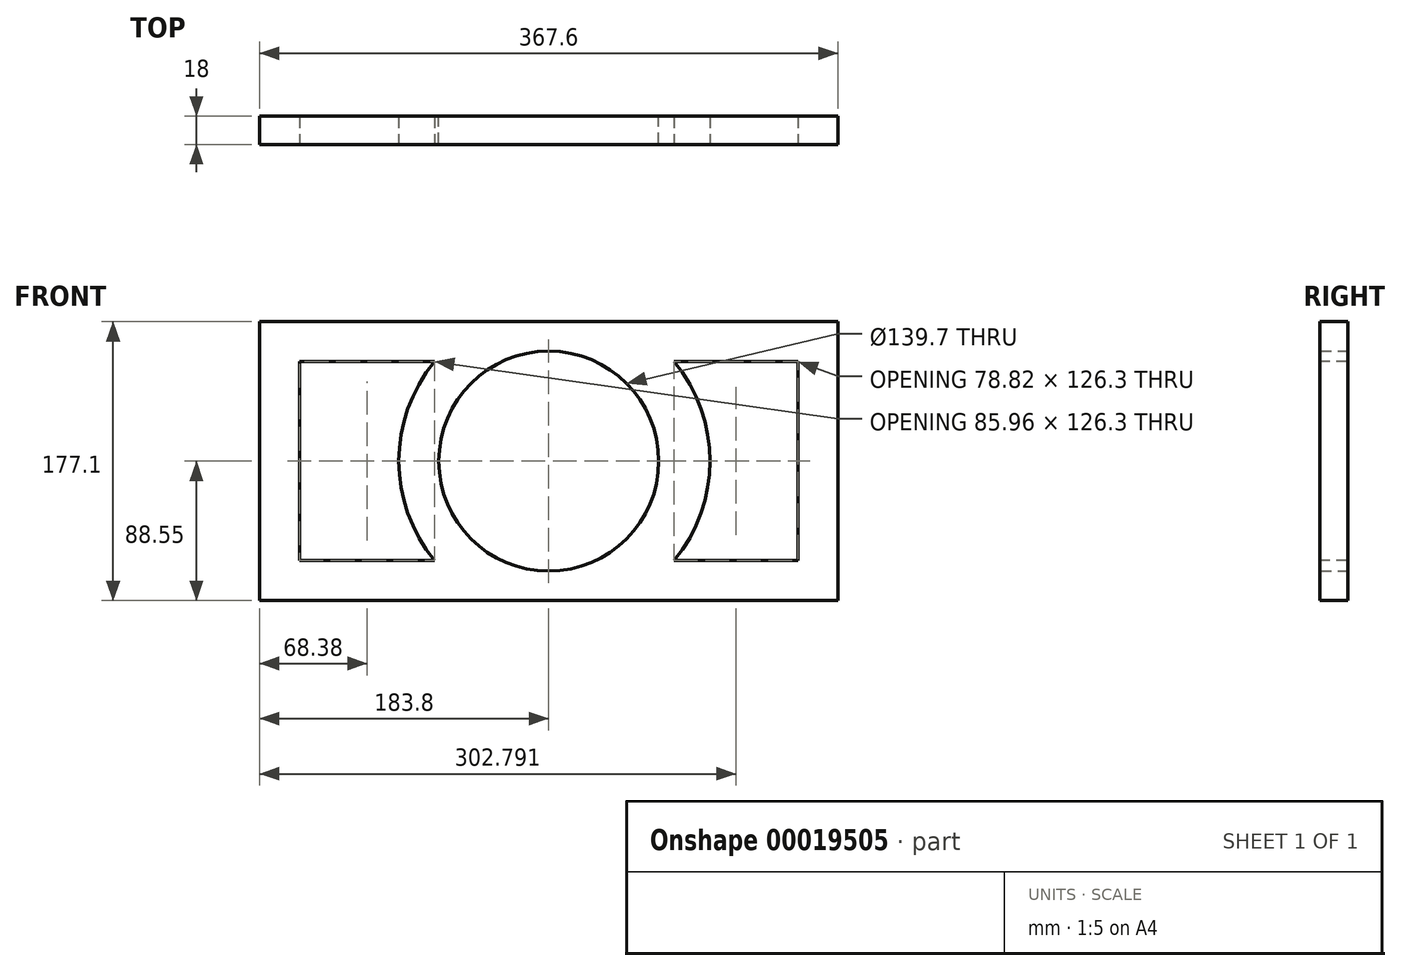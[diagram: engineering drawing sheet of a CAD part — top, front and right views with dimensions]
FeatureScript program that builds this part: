
annotation { "Feature Type Name" : "Feature", "Feature Type Description" : "" }
export const myFeature = defineFeature(function(context is Context, id is Id, definition is map)
    precondition{}
    {
        {
            var Q0;
            Q0=qCreatedBy(makeId("Front.planeOp"),FACE);
            var sketch = newSketch(context, id + "F0", { "sketchPlane" : qUnion([Q0])});
            skLineSegment(sketch, "E0.rect.bottom", {"start": v(183.8, 88.55) * mm, "end": v(-183.8, 88.55) * mm});
            skLineSegment(sketch, "E0.rect.top", {"start": v(183.8, -88.55) * mm, "end": v(-183.8, -88.55) * mm});
            skLineSegment(sketch, "E0.rect.left", {"start": v(183.8, 88.55) * mm, "end": v(183.8, -88.55) * mm});
            skLineSegment(sketch, "E0.rect.right", {"start": v(-183.8, 88.55) * mm, "end": v(-183.8, -88.55) * mm});
            skPoint(sketch, "E0.rect.middle", {"position": v(0, 0) * mm});
            skSolve(sketch);
        }
        {
            var Q0;
            Q0 = qSketchRegion(id + "F0", true);
            extrude(context, id + "F1", {"entities" : qUnion([Q0]), "depth" : 18 * mm});
        }
        {
            var Q0;
            Q0=makeQuery(id+"F1.opExtrude","CAP_FACE",FACE,{"disambiguationData":[OSD([sQuery(id+"F0.wireOp",EDGE,"E0.rect.bottom"),sQuery(id+"F0.wireOp",EDGE,"E0.rect.top"),sQuery(id+"F0.wireOp",EDGE,"E0.rect.left"),sQuery(id+"F0.wireOp",EDGE,"E0.rect.right")])],"isStart":false});
            var sketch = newSketch(context, id + "F2", { "sketchPlane" : qUnion([Q0])});
            skPoint(sketch, "E1", {"position": v(0, 0) * mm});
            skSolve(sketch);
        }
        {
            var Q0;
            Q0=sQuery(id+"F2.wireOp",VERTEX,"E1");
            var Q1;
            Q1=makeQuery(id+"F1.opExtrude","SWEPT_BODY",BODY,{"disambiguationData":[OSD([sQuery(id+"F0.wireOp",EDGE,"E0.rect.bottom"),sQuery(id+"F0.wireOp",EDGE,"E0.rect.top"),sQuery(id+"F0.wireOp",EDGE,"E0.rect.left"),sQuery(id+"F0.wireOp",EDGE,"E0.rect.right")])]});
            hole(context, id + "F3", {"style" : HoleStyle.SIMPLE, "holeDiameter" : 139.7 * mm, "endStyle" : HoleEndStyle.THROUGH, "locations" : qUnion([Q0]), "scope" : qUnion([Q1])});
        }
        {
            var Q0;
            Q0=makeQuery(id+"F1.opExtrude","CAP_FACE",FACE,{"disambiguationData":[OSD([sQuery(id+"F0.wireOp",EDGE,"E0.rect.bottom"),sQuery(id+"F0.wireOp",EDGE,"E0.rect.top"),sQuery(id+"F0.wireOp",EDGE,"E0.rect.left"),sQuery(id+"F0.wireOp",EDGE,"E0.rect.right")])],"isStart":false});
            var sketch = newSketch(context, id + "F4", { "sketchPlane" : qUnion([Q0])});
            skArc(sketch, "E2", {"start": v(-72.44, 63.15) * mm, "mid": v(-95.25, 0) * mm, "end": v(-72.44, -63.15) * mm});
            skLineSegment(sketch, "E3.rect.bottom", {"start": v(-158.4, 63.15) * mm, "end": v(-72.44, 63.15) * mm});
            skLineSegment(sketch, "E3.rect.top", {"start": v(-158.4, -63.15) * mm, "end": v(-72.44, -63.15) * mm});
            skLineSegment(sketch, "E3.rect.left", {"start": v(-158.4, 63.15) * mm, "end": v(-158.4, -63.15) * mm});
            skLineSegment(sketch, "E3.rect.right", {"start": v(158.4, 63.15) * mm, "end": v(158.4, -63.15) * mm});
            skPoint(sketch, "E3.rect.middle", {"position": v(0, 0) * mm});
            skArc(sketch, "E4.trimOffspring", {"start": v(79.58, -63.15) * mm, "mid": v(102.4, 0) * mm, "end": v(79.58, 63.15) * mm});
            skLineSegment(sketch, "E5.trimOffspring", {"start": v(79.58, -63.15) * mm, "end": v(158.4, -63.15) * mm});
            skLineSegment(sketch, "E6.trimOffspring", {"start": v(79.58, 63.15) * mm, "end": v(158.4, 63.15) * mm});
            skSolve(sketch);
        }
        {
            var Q0;
            Q0 = qSketchRegion(id + "F4", true);
            extrude(context, id + "F5", {"entities" : qUnion([Q0]), "operationType" : NewBodyOperationType.REMOVE, "oppositeDirection" : true, "depth" : 25.4 * mm});
        }
    });
